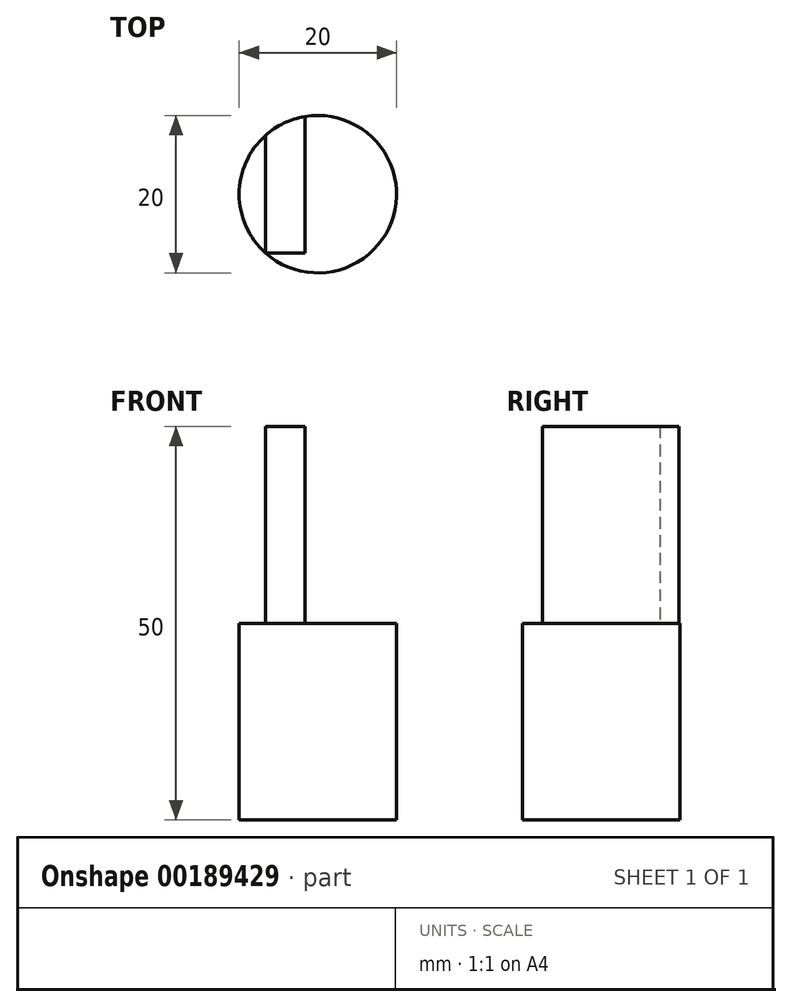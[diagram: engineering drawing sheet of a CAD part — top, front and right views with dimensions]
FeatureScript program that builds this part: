
annotation { "Feature Type Name" : "Feature", "Feature Type Description" : "" }
export const myFeature = defineFeature(function(context is Context, id is Id, definition is map)
    precondition{}
    {
        {
            var Q0;
            Q0=qCreatedBy(makeId("Top.planeOp"),FACE);
            var sketch = newSketch(context, id + "F0", { "sketchPlane" : qUnion([Q0])});
            skCircle(sketch, "E0", {"center": v(0, 0) * mm, "radius": 10 * mm});
            skSolve(sketch);
        }
        {
            var Q0;
            Q0=makeQuery(id+"F0.imprint","IMPRINT",FACE,{"disambiguationData":[TD([[makeQuery(id+"F0.imprint","IMPRINT",EDGE,{"derivedFrom":sQuery(id+"F0.wireOp",EDGE,"E0")}),1.0]])]});
            extrude(context, id + "F1", {"entities" : qUnion([Q0]), "depth" : 25 * mm});
        }
        {
            var Q0;
            Q0=makeQuery(id+"F1.opExtrude","CAP_FACE",FACE,{"disambiguationData":[OSD([sQuery(id+"F0.wireOp",EDGE,"E0")])],"isStart":false});
            var sketch = newSketch(context, id + "F2", { "sketchPlane" : qUnion([Q0])});
            skLineSegment(sketch, "E1.bottom", {"start": v(-6.66, -7.46) * mm, "end": v(-1.66, -7.46) * mm});
            skLineSegment(sketch, "E1.top", {"start": v(-6.66, 9.86) * mm, "end": v(-1.66, 9.86) * mm});
            skLineSegment(sketch, "E1.left", {"start": v(-6.66, -7.46) * mm, "end": v(-6.66, 9.86) * mm});
            skLineSegment(sketch, "E1.right", {"start": v(-1.66, -7.46) * mm, "end": v(-1.66, 9.86) * mm});
            skSolve(sketch);
        }
        {
            var Q0;
            {var subQ0=sQuery(id+"F2.wireOp",EDGE,"E1.bottom");Q0=makeQuery(id+"F2.imprint","IMPRINT",FACE,{"disambiguationData":[TD([[makeQuery(id+"F2.imprint","IMPRINT",EDGE,{"derivedFrom":subQ0}),1.0]])]});}
            extrude(context, id + "F3", {"entities" : qUnion([Q0]), "operationType" : NewBodyOperationType.ADD, "depth" : 25 * mm});
        }
    });
